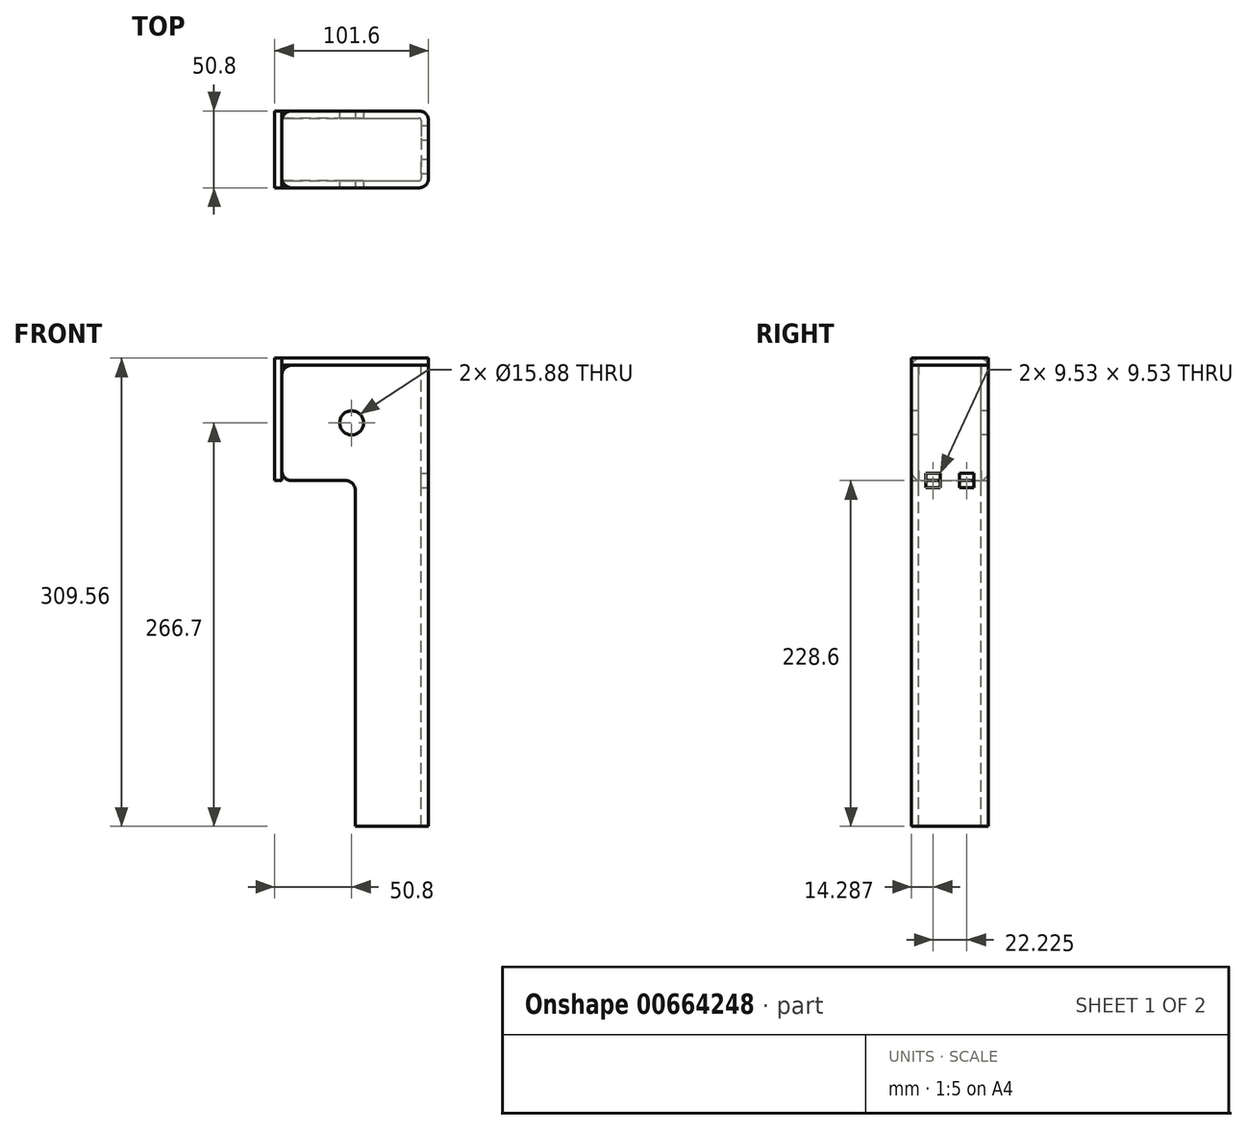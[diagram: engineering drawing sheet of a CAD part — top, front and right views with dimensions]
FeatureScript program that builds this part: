
annotation { "Feature Type Name" : "Feature", "Feature Type Description" : "" }
export const myFeature = defineFeature(function(context is Context, id is Id, definition is map)
    precondition{}
    {
        {
            var Q0;
            Q0=qCreatedBy(makeId("Top.planeOp"),FACE);
            var sketch = newSketch(context, id + "F0", { "sketchPlane" : qUnion([Q0])});
            skLineSegment(sketch, "E0.bottom", {"start": v(-46.04, 20.64) * mm, "end": v(46.04, 20.64) * mm});
            skLineSegment(sketch, "E0.top", {"start": v(-46.04, -20.64) * mm, "end": v(46.04, -20.64) * mm});
            skLineSegment(sketch, "E0.right", {"start": v(46.04, 20.64) * mm, "end": v(46.04, -20.64) * mm});
            skPoint(sketch, "E0.middle", {"position": v(0, 0) * mm});
            skLineSegment(sketch, "E1.0", {"start": v(-46.04, 25.4) * mm, "end": v(50.8, 25.4) * mm});
            skLineSegment(sketch, "E1.2", {"start": v(-46.04, -25.4) * mm, "end": v(50.8, -25.4) * mm});
            skLineSegment(sketch, "E1.3", {"start": v(50.8, 25.4) * mm, "end": v(50.8, -25.4) * mm});
            skPoint(sketch, "E2.visualSharp", {"position": v(46.04, 20.64) * mm});
            skPoint(sketch, "E3.visualSharp", {"position": v(46.04, -20.64) * mm});
            skPoint(sketch, "E4.visualSharp", {"position": v(50.8, 25.4) * mm});
            skPoint(sketch, "E5.visualSharp", {"position": v(50.8, -25.4) * mm});
            skLineSegment(sketch, "E6", {"start": v(-46.04, 25.4) * mm, "end": v(-46.04, 20.64) * mm});
            skLineSegment(sketch, "E7", {"start": v(-46.04, -20.64) * mm, "end": v(-46.04, -25.4) * mm});
            skSolve(sketch);
        }
        {
            var Q0;
            Q0 = qSketchRegion(id + "F0", true);
            extrude(context, id + "F1", {"entities" : qUnion([Q0]), "oppositeDirection" : true, "depth" : 304.8 * mm, "offsetDistance" : 25.4 * mm});
        }
        {
            var Q0;
            Q0=makeQuery(id+"F1.opExtrude","SWEPT_FACE",FACE,{"disambiguationData":[OSD([sQuery(id+"F0.wireOp",EDGE,"E1.3")])]});
            var sketch = newSketch(context, id + "F2", { "sketchPlane" : qUnion([Q0])});
            skLineSegment(sketch, "E8.bottom", {"start": v(-6.35, -71.44) * mm, "end": v(-15.87, -71.44) * mm});
            skLineSegment(sketch, "E8.top", {"start": v(-6.35, -80.96) * mm, "end": v(-15.87, -80.96) * mm});
            skLineSegment(sketch, "E8.left", {"start": v(-6.35, -71.44) * mm, "end": v(-6.35, -80.96) * mm});
            skLineSegment(sketch, "E8.right", {"start": v(-15.87, -71.44) * mm, "end": v(-15.87, -80.96) * mm});
            skPoint(sketch, "E8.middle", {"position": v(-11.11, -76.2) * mm});
            skLineSegment(sketch, "E9.bottom", {"start": v(6.35, -71.44) * mm, "end": v(15.88, -71.44) * mm});
            skLineSegment(sketch, "E9.top", {"start": v(6.35, -80.96) * mm, "end": v(15.88, -80.96) * mm});
            skLineSegment(sketch, "E9.left", {"start": v(6.35, -71.44) * mm, "end": v(6.35, -80.96) * mm});
            skLineSegment(sketch, "E9.right", {"start": v(15.88, -71.44) * mm, "end": v(15.88, -80.96) * mm});
            skPoint(sketch, "E9.middle", {"position": v(11.11, -76.2) * mm});
            skSolve(sketch);
        }
        {
            var Q0;
            Q0 = qSketchRegion(id + "F2", true);
            extrude(context, id + "F3", {"entities" : qUnion([Q0]), "operationType" : NewBodyOperationType.REMOVE, "endBound" : BoundingType.THROUGH_ALL, "oppositeDirection" : true, "depth" : 25.4 * mm, "offsetDistance" : 25.4 * mm});
        }
        {
            var Q0;
            Q0=makeQuery(id+"F1.opExtrude","SWEPT_FACE",FACE,{"disambiguationData":[OSD([sQuery(id+"F0.wireOp",EDGE,"E1.2")])]});
            var sketch = newSketch(context, id + "F4", { "sketchPlane" : qUnion([Q0])});
            skLineSegment(sketch, "E10.bottom", {"start": v(2.38, -304.8) * mm, "end": v(-104.52, -304.8) * mm});
            skLineSegment(sketch, "E10.top", {"start": v(2.38, -76.2) * mm, "end": v(-104.52, -76.2) * mm});
            skLineSegment(sketch, "E10.left", {"start": v(2.38, -304.8) * mm, "end": v(2.38, -76.2) * mm});
            skLineSegment(sketch, "E10.right", {"start": v(-104.52, -304.8) * mm, "end": v(-104.52, -76.2) * mm});
            skSolve(sketch);
        }
        {
            var Q0;
            Q0 = qSketchRegion(id + "F4", true);
            extrude(context, id + "F5", {"entities" : qUnion([Q0]), "operationType" : NewBodyOperationType.REMOVE, "oppositeDirection" : true, "depth" : 50.8 * mm, "offsetDistance" : 25.4 * mm});
        }
        {
            var Q0;
            Q0=qCreatedBy(makeId("Top.planeOp"),FACE);
            var sketch = newSketch(context, id + "F6", { "sketchPlane" : qUnion([Q0])});
            skLineSegment(sketch, "E11.0", {"start": v(-46.04, 25.4) * mm, "end": v(50.8, 25.4) * mm});
            skLineSegment(sketch, "E12.0", {"start": v(50.8, 25.4) * mm, "end": v(50.8, -25.4) * mm});
            skLineSegment(sketch, "E13.0", {"start": v(-46.04, -25.4) * mm, "end": v(50.8, -25.4) * mm});
            skLineSegment(sketch, "E14", {"start": v(-46.04, 25.4) * mm, "end": v(-46.04, -25.4) * mm});
            skSolve(sketch);
        }
        {
            var Q0;
            Q0 = qSketchRegion(id + "F6", true);
            extrude(context, id + "F7", {"entities" : qUnion([Q0]), "depth" : 4.76 * mm, "offsetDistance" : 25.4 * mm});
        }
        {
            var Q0;
            Q0=makeQuery(id+"F1.opExtrude","SWEPT_FACE",FACE,{"disambiguationData":[OSD([sQuery(id+"F0.wireOp",EDGE,"E6")])]});
            var sketch = newSketch(context, id + "F8", { "sketchPlane" : qUnion([Q0])});
            skLineSegment(sketch, "E15.0", {"start": v(-25.4, -76.2) * mm, "end": v(-25.4, 0) * mm});
            skLineSegment(sketch, "E16.0", {"start": v(25.4, -76.2) * mm, "end": v(25.4, 0) * mm});
            skLineSegment(sketch, "E17.0", {"start": v(-25.4, 4.76) * mm, "end": v(25.4, 4.76) * mm});
            skLineSegment(sketch, "E18", {"start": v(-25.4, 4.76) * mm, "end": v(-25.4, 0) * mm});
            skLineSegment(sketch, "E19", {"start": v(25.4, 4.76) * mm, "end": v(25.4, 0) * mm});
            skLineSegment(sketch, "E20", {"start": v(-25.4, -76.2) * mm, "end": v(25.4, -76.2) * mm});
            skSolve(sketch);
        }
        {
            var Q0;
            Q0 = qSketchRegion(id + "F8", true);
            extrude(context, id + "F9", {"entities" : qUnion([Q0]), "depth" : 4.76 * mm, "offsetDistance" : 25.4 * mm});
        }
        {
            var Q0;
            Q0=makeQuery(id+"F1.opExtrude","SWEPT_FACE",FACE,{"disambiguationData":[OSD([sQuery(id+"F0.wireOp",EDGE,"E1.2")])]});
            var sketch = newSketch(context, id + "F10", { "sketchPlane" : qUnion([Q0])});
            skCircle(sketch, "E21", {"center": v(0, -38.1) * mm, "radius": 7.94 * mm});
            skPoint(sketch, "E21.centerSnap0", {"position": v(-46.04, -38.1) * mm});
            skSolve(sketch);
        }
        {
            var Q0;
            Q0 = qSketchRegion(id + "F10", true);
            var Q1;
            Q1=makeQuery(id+"F1.opExtrude","SWEPT_FACE",FACE,{"disambiguationData":[OSD([sQuery(id+"F0.wireOp",EDGE,"E1.0")])]});
            extrude(context, id + "F11", {"entities" : qUnion([Q0]), "operationType" : NewBodyOperationType.REMOVE, "endBound" : BoundingType.UP_TO_SURFACE, "oppositeDirection" : true, "depth" : 25.4 * mm, "endBoundEntityFace" : qUnion([Q1]), "offsetDistance" : 25.4 * mm});
        }
        {
            var Q0;
            Q0=makeQuery(id+"F9.opExtrude","SWEPT_EDGE",EDGE,{"disambiguationData":[OSD([sQuery(id+"F8.wireOp",EDGE,"E17.0"),sQuery(id+"F8.wireOp",EDGE,"E19")])]});
            var Q1;
            Q1=makeQuery(id+"F9.opExtrude","SWEPT_EDGE",EDGE,{"disambiguationData":[OSD([sQuery(id+"F8.wireOp",EDGE,"E17.0"),sQuery(id+"F8.wireOp",EDGE,"E18")])]});
            var Q2;
            Q2=makeQuery(id+"F9.opExtrude","SWEPT_EDGE",EDGE,{"disambiguationData":[OSD([sQuery(id+"F8.wireOp",EDGE,"E16.0"),sQuery(id+"F8.wireOp",EDGE,"E20")])]});
            var Q3;
            Q3=makeQuery(id+"F9.opExtrude","SWEPT_EDGE",EDGE,{"disambiguationData":[OSD([sQuery(id+"F8.wireOp",EDGE,"E15.0"),sQuery(id+"F8.wireOp",EDGE,"E20")])]});
            var Q4;
            Q4=makeQuery(id+"F7.opExtrude","SWEPT_EDGE",EDGE,{"disambiguationData":[OSD([sQuery(id+"F6.wireOp",EDGE,"E11.0"),sQuery(id+"F6.wireOp",EDGE,"E14")])]});
            var Q5;
            Q5=makeQuery(id+"F7.opExtrude","SWEPT_EDGE",EDGE,{"disambiguationData":[OSD([sQuery(id+"F6.wireOp",EDGE,"E13.0"),sQuery(id+"F6.wireOp",EDGE,"E14")])]});
            var Q6;
            Q6=makeQuery(id+"F7.opExtrude","SWEPT_EDGE",EDGE,{"disambiguationData":[OSD([sQuery(id+"F6.wireOp",EDGE,"E12.0"),sQuery(id+"F6.wireOp",EDGE,"E13.0")])]});
            var Q7;
            Q7=makeQuery(id+"F7.opExtrude","SWEPT_EDGE",EDGE,{"disambiguationData":[OSD([sQuery(id+"F6.wireOp",EDGE,"E11.0"),sQuery(id+"F6.wireOp",EDGE,"E12.0")])]});
            fillet(context, id + "F12", {"entities" : qUnion([Q0, Q1, Q2, Q3, Q4, Q5, Q6, Q7]), "tangentPropagation" : true, "radius" : 6.35 * mm, "defaultsChanged" : true, "vertexSettings" : [], "allowEdgeOverflow" : false});
        }
        {
            var Q0;
            Q0=makeQuery(id+"F1.opExtrude","SWEPT_EDGE",EDGE,{"disambiguationData":[OSD([sQuery(id+"F0.wireOp",EDGE,"E1.2"),sQuery(id+"F0.wireOp",EDGE,"E1.3")])]});
            var Q1;
            Q1=makeQuery(id+"F1.opExtrude","SWEPT_EDGE",EDGE,{"disambiguationData":[OSD([sQuery(id+"F0.wireOp",EDGE,"E1.0"),sQuery(id+"F0.wireOp",EDGE,"E1.3")])]});
            var Q2;
            {var subQ0=sQuery(id+"F4.wireOp",EDGE,"E10.top");var subQ1=sQuery(id+"F4.wireOp",EDGE,"E10.left");Q2=makeQuery(id+"F5.boolean.opBoolean","COPY",EDGE,{"disambiguationData":[TD([makeQuery(id+"F1.opExtrude","SWEPT_FACE",FACE,{"disambiguationData":[OSD([sQuery(id+"F0.wireOp",EDGE,"E0.bottom")])]})])],"derivedFrom":makeQuery(id+"F5.opExtrude","SWEPT_EDGE",EDGE,{"disambiguationData":[OSD([subQ0,subQ1])]})});}
            var Q3;
            {var subQ0=sQuery(id+"F4.wireOp",EDGE,"E10.left");var subQ1=sQuery(id+"F4.wireOp",EDGE,"E10.top");Q3=makeQuery(id+"F5.boolean.opBoolean","COPY",EDGE,{"disambiguationData":[TD([makeQuery(id+"F1.opExtrude","SWEPT_FACE",FACE,{"disambiguationData":[OSD([sQuery(id+"F0.wireOp",EDGE,"E0.top")])]})])],"derivedFrom":makeQuery(id+"F5.opExtrude","SWEPT_EDGE",EDGE,{"disambiguationData":[OSD([subQ1,subQ0])]})});}
            var Q4;
            Q4=makeQuery(id+"F5.boolean.opBoolean","INTERSECT",EDGE,{"derivedFrom":[makeQuery(id+"F1.opExtrude","SWEPT_FACE",FACE,{"disambiguationData":[OSD([sQuery(id+"F0.wireOp",EDGE,"E6")])]}),makeQuery(id+"F5.opExtrude","SWEPT_FACE",FACE,{"disambiguationData":[OSD([sQuery(id+"F4.wireOp",EDGE,"E10.top")])]})]});
            var Q5;
            Q5=makeQuery(id+"F5.boolean.opBoolean","INTERSECT",EDGE,{"derivedFrom":[makeQuery(id+"F1.opExtrude","SWEPT_FACE",FACE,{"disambiguationData":[OSD([sQuery(id+"F0.wireOp",EDGE,"E7")])]}),makeQuery(id+"F5.opExtrude","SWEPT_FACE",FACE,{"disambiguationData":[OSD([sQuery(id+"F4.wireOp",EDGE,"E10.top")])]})]});
            var Q6;
            Q6=makeQuery(id+"F1.opExtrude","CAP_EDGE",EDGE,{"disambiguationData":[OSD([sQuery(id+"F0.wireOp",EDGE,"E7")])],"isStart":true});
            var Q7;
            Q7=makeQuery(id+"F1.opExtrude","CAP_EDGE",EDGE,{"disambiguationData":[OSD([sQuery(id+"F0.wireOp",EDGE,"E6")])],"isStart":true});
            fillet(context, id + "F13", {"entities" : qUnion([Q0, Q1, Q2, Q3, Q4, Q5, Q6, Q7]), "tangentPropagation" : true, "radius" : 6.35 * mm, "defaultsChanged" : true, "vertexSettings" : [], "allowEdgeOverflow" : false});
        }
        {
            var Q0;
            Q0=makeQuery(id+"F1.opExtrude","SWEPT_EDGE",EDGE,{"disambiguationData":[OSD([sQuery(id+"F0.wireOp",EDGE,"E0.bottom"),sQuery(id+"F0.wireOp",EDGE,"E0.right")])]});
            var Q1;
            Q1=makeQuery(id+"F1.opExtrude","SWEPT_EDGE",EDGE,{"disambiguationData":[OSD([sQuery(id+"F0.wireOp",EDGE,"E0.top"),sQuery(id+"F0.wireOp",EDGE,"E0.right")])]});
            fillet(context, id + "F14", {"entities" : qUnion([Q0, Q1]), "tangentPropagation" : true, "radius" : 1.59 * mm, "defaultsChanged" : true, "vertexSettings" : [], "allowEdgeOverflow" : false});
        }
    });
